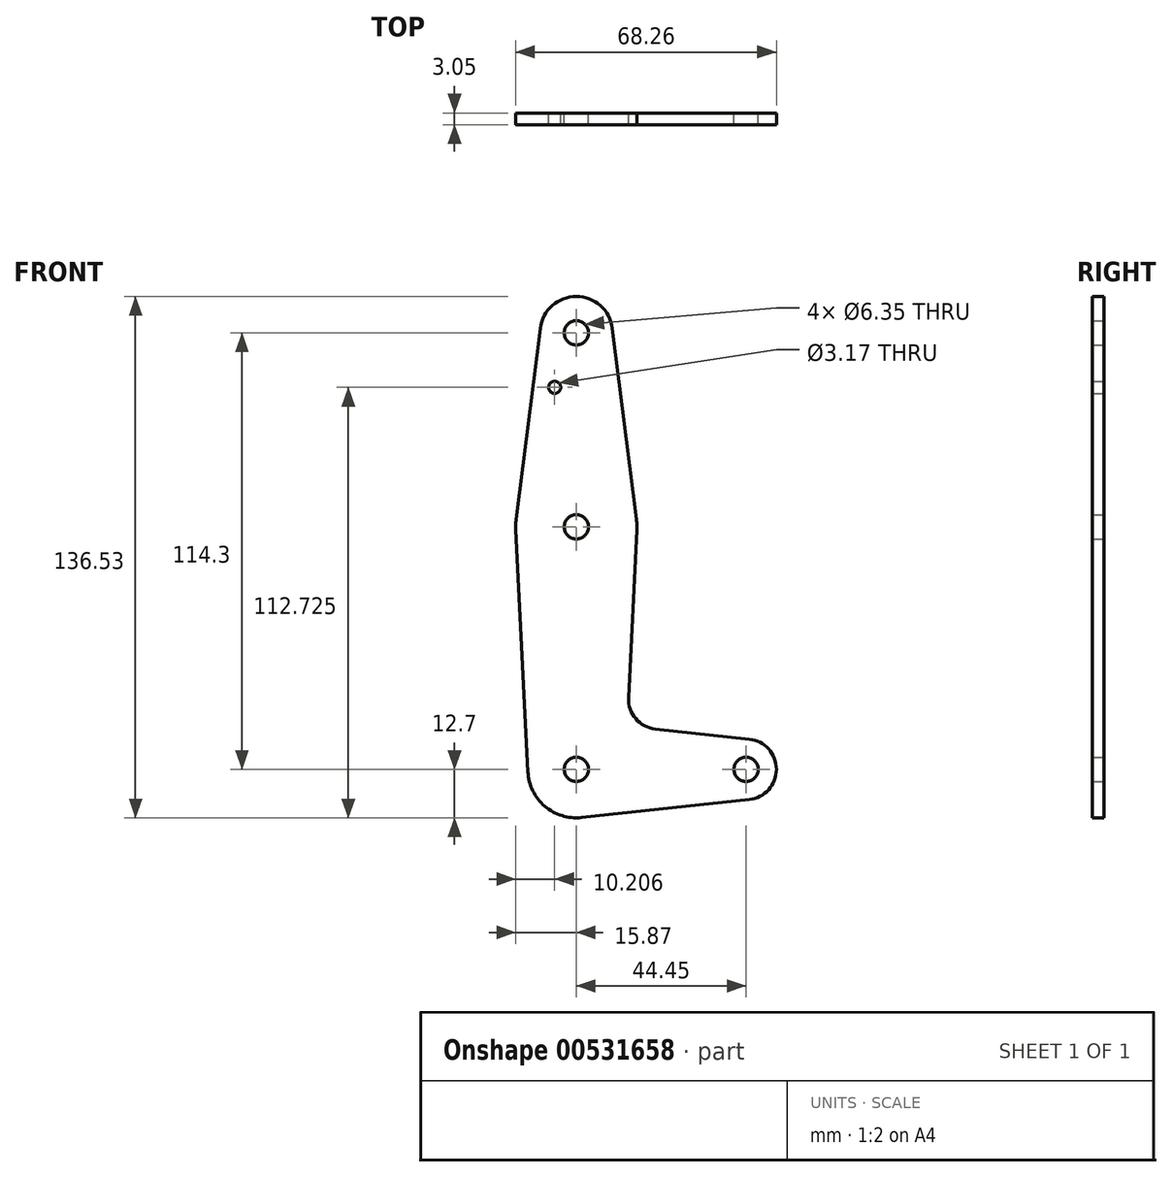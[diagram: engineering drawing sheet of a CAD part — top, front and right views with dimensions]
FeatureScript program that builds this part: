
annotation { "Feature Type Name" : "Feature", "Feature Type Description" : "" }
export const myFeature = defineFeature(function(context is Context, id is Id, definition is map)
    precondition{}
    {
        {
            var Q0;
            Q0=qCreatedBy(makeId("Front.planeOp"),FACE);
            var sketch = newSketch(context, id + "F0", { "sketchPlane" : qUnion([Q0])});
            skCircle(sketch, "E0", {"center": v(0, 0) * mm, "radius": 12.7 * mm});
            skCircle(sketch, "E1", {"center": v(0, 63.5) * mm, "radius": 15.88 * mm});
            skCircle(sketch, "E2", {"center": v(0, 114.3) * mm, "radius": 9.53 * mm});
            skCircle(sketch, "E3", {"center": v(44.45, 0) * mm, "radius": 7.94 * mm});
            skLineSegment(sketch, "E4", {"start": v(0, 114.3) * mm, "end": v(0, 63.5) * mm, "construction": true});
            skLineSegment(sketch, "E5", {"start": v(0, 63.5) * mm, "end": v(0, 0) * mm, "construction": true});
            skLineSegment(sketch, "E6", {"start": v(0, 0) * mm, "end": v(44.45, 0) * mm, "construction": true});
            skLineSegment(sketch, "E7", {"start": v(-9.45, 115.5) * mm, "end": v(-15.75, 65.48) * mm});
            skLineSegment(sketch, "E8", {"start": v(9.45, 115.5) * mm, "end": v(15.75, 65.48) * mm});
            skLineSegment(sketch, "E9", {"start": v(15.86, 62.7) * mm, "end": v(13.66, 18.84) * mm});
            skLineSegment(sketch, "E10", {"start": v(-15.86, 62.7) * mm, "end": v(-12.68, -0.64) * mm});
            skLineSegment(sketch, "E11", {"start": v(45.3, -7.9) * mm, "end": v(1.36, -12.63) * mm});
            skLineSegment(sketch, "E12", {"start": v(20.75, 10.54) * mm, "end": v(45.3, 7.9) * mm});
            skCircle(sketch, "E13", {"center": v(0, 114.3) * mm, "radius": 3.18 * mm});
            skCircle(sketch, "E14", {"center": v(0, 63.5) * mm, "radius": 3.18 * mm});
            skCircle(sketch, "E15", {"center": v(0, 0) * mm, "radius": 3.18 * mm});
            skCircle(sketch, "E16", {"center": v(44.45, 0) * mm, "radius": 3.18 * mm});
            skCircle(sketch, "E17", {"center": v(-5.66, 100.03) * mm, "radius": 1.59 * mm});
            skArc(sketch, "E18.filletArc", {"start": v(13.66, 18.84) * mm, "mid": v(15.55, 13.28) * mm, "end": v(20.75, 10.54) * mm});
            skSolve(sketch);
        }
        {
            var Q0;
            {var subQ1=sQuery(id+"F0.wireOp",EDGE,"E7");Q0=makeQuery(id+"F0.imprint","IMPRINT",FACE,{"disambiguationData":[TD([[makeQuery(id+"F0.imprint","IMPRINT",EDGE,{"derivedFrom":subQ1}),1.0]])]});}
            var Q1;
            Q1=makeQuery(id+"F0.imprint","IMPRINT",FACE,{"disambiguationData":[TD([[makeQuery(id+"F0.imprint","IMPRINT",EDGE,{"derivedFrom":sQuery(id+"F0.wireOp",EDGE,"E14")}),-1.0]])]});
            var Q2;
            {var subQ0=sQuery(id+"F0.wireOp",EDGE,"E9");Q2=makeQuery(id+"F0.imprint","IMPRINT",FACE,{"disambiguationData":[TD([[makeQuery(id+"F0.imprint","IMPRINT",EDGE,{"derivedFrom":subQ0}),-1.0]])]});}
            var Q3;
            Q3=makeQuery(id+"F0.imprint","IMPRINT",FACE,{"disambiguationData":[TD([[makeQuery(id+"F0.imprint","IMPRINT",EDGE,{"derivedFrom":sQuery(id+"F0.wireOp",EDGE,"E15")}),-1.0]])]});
            var Q4;
            Q4=makeQuery(id+"F0.imprint","IMPRINT",FACE,{"disambiguationData":[TD([[makeQuery(id+"F0.imprint","IMPRINT",EDGE,{"derivedFrom":sQuery(id+"F0.wireOp",EDGE,"E16")}),-1.0]])]});
            var Q5;
            Q5=makeQuery(id+"F0.imprint","IMPRINT",FACE,{"disambiguationData":[TD([[makeQuery(id+"F0.imprint","IMPRINT",EDGE,{"derivedFrom":sQuery(id+"F0.wireOp",EDGE,"E13")}),-1.0]])]});
            extrude(context, id + "F1", {"entities" : qUnion([Q0, Q1, Q2, Q3, Q4, Q5]), "depth" : 3.05 * mm, "offsetDistance" : 25.4 * mm});
        }
    });
